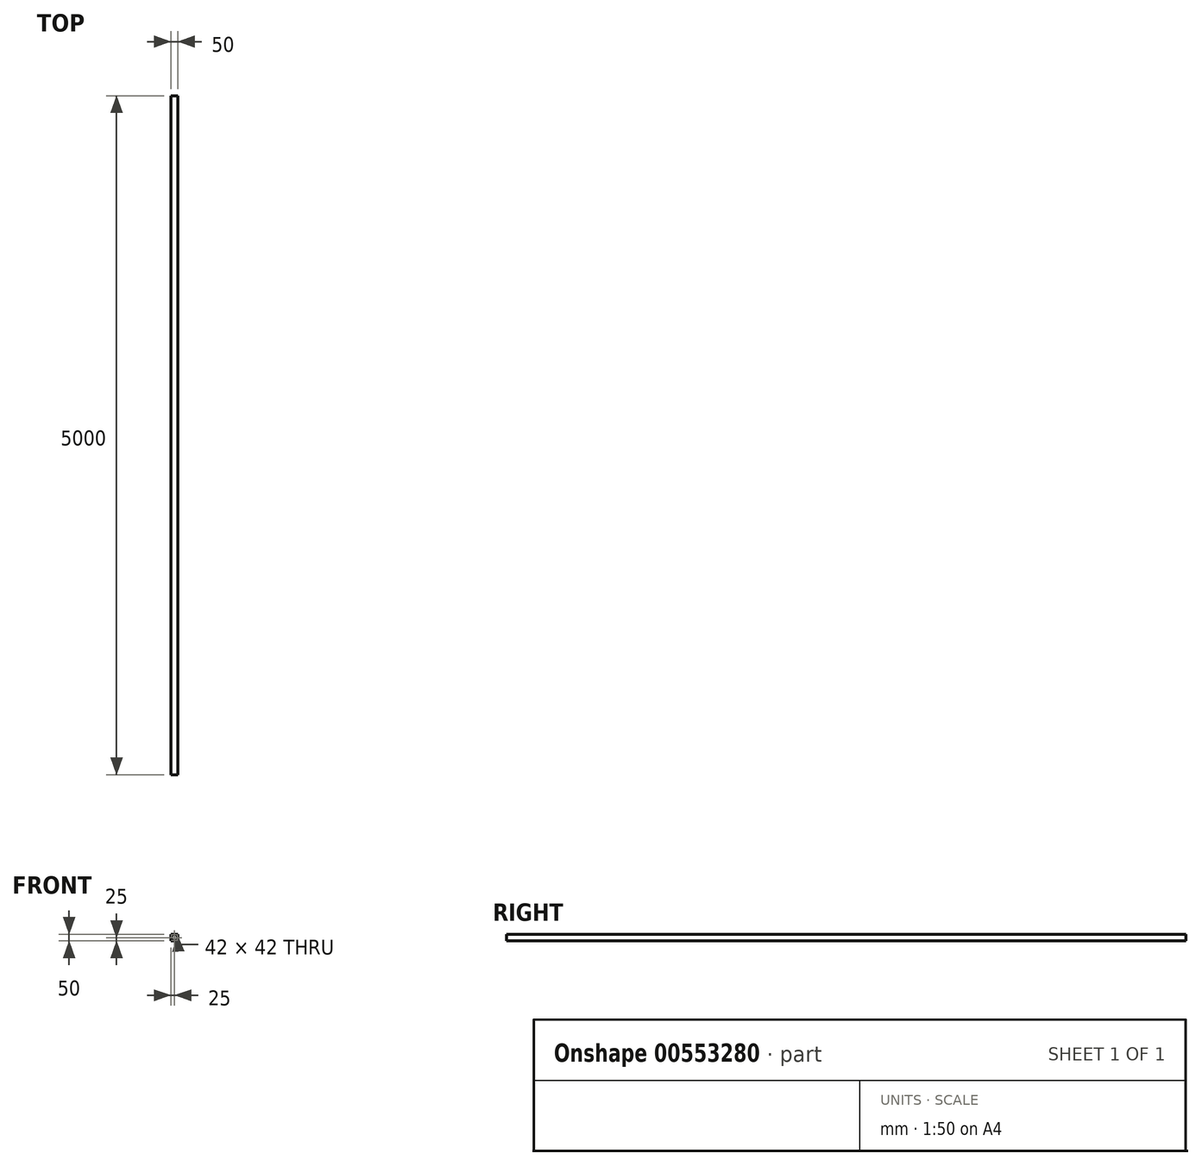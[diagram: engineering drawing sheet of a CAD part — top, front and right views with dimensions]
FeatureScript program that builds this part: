
annotation { "Feature Type Name" : "Feature", "Feature Type Description" : "" }
export const myFeature = defineFeature(function(context is Context, id is Id, definition is map)
    precondition{}
    {
        {
            var Q0;
            Q0=qCreatedBy(makeId("Front.planeOp"),FACE);
            var sketch = newSketch(context, id + "F0", { "sketchPlane" : qUnion([Q0])});
            skLineSegment(sketch, "E0.bottom", {"start": v(-25, -25) * mm, "end": v(25, -25) * mm});
            skLineSegment(sketch, "E0.top", {"start": v(-25, 25) * mm, "end": v(25, 25) * mm});
            skLineSegment(sketch, "E0.left", {"start": v(-25, -25) * mm, "end": v(-25, 25) * mm});
            skLineSegment(sketch, "E0.right", {"start": v(25, -25) * mm, "end": v(25, 25) * mm});
            skPoint(sketch, "E0.middle", {"position": v(0, 0) * mm});
            skLineSegment(sketch, "E1.bottom", {"start": v(21, -21) * mm, "end": v(-21, -21) * mm});
            skLineSegment(sketch, "E1.top", {"start": v(21, 21) * mm, "end": v(-21, 21) * mm});
            skLineSegment(sketch, "E1.left", {"start": v(21, -21) * mm, "end": v(21, 21) * mm});
            skLineSegment(sketch, "E1.right", {"start": v(-21, -21) * mm, "end": v(-21, 21) * mm});
            skSolve(sketch);
        }
        {
            var Q0;
            Q0=makeQuery(id+"F0.imprint","IMPRINT",FACE,{"disambiguationData":[TD([[makeQuery(id+"F0.imprint","IMPRINT",EDGE,{"derivedFrom":sQuery(id+"F0.wireOp",EDGE,"E0.bottom")}),1.0]])]});
            extrude(context, id + "F1", {"entities" : qUnion([Q0]), "depth" : 5000 * mm, "offsetDistance" : 25 * mm});
        }
    });
